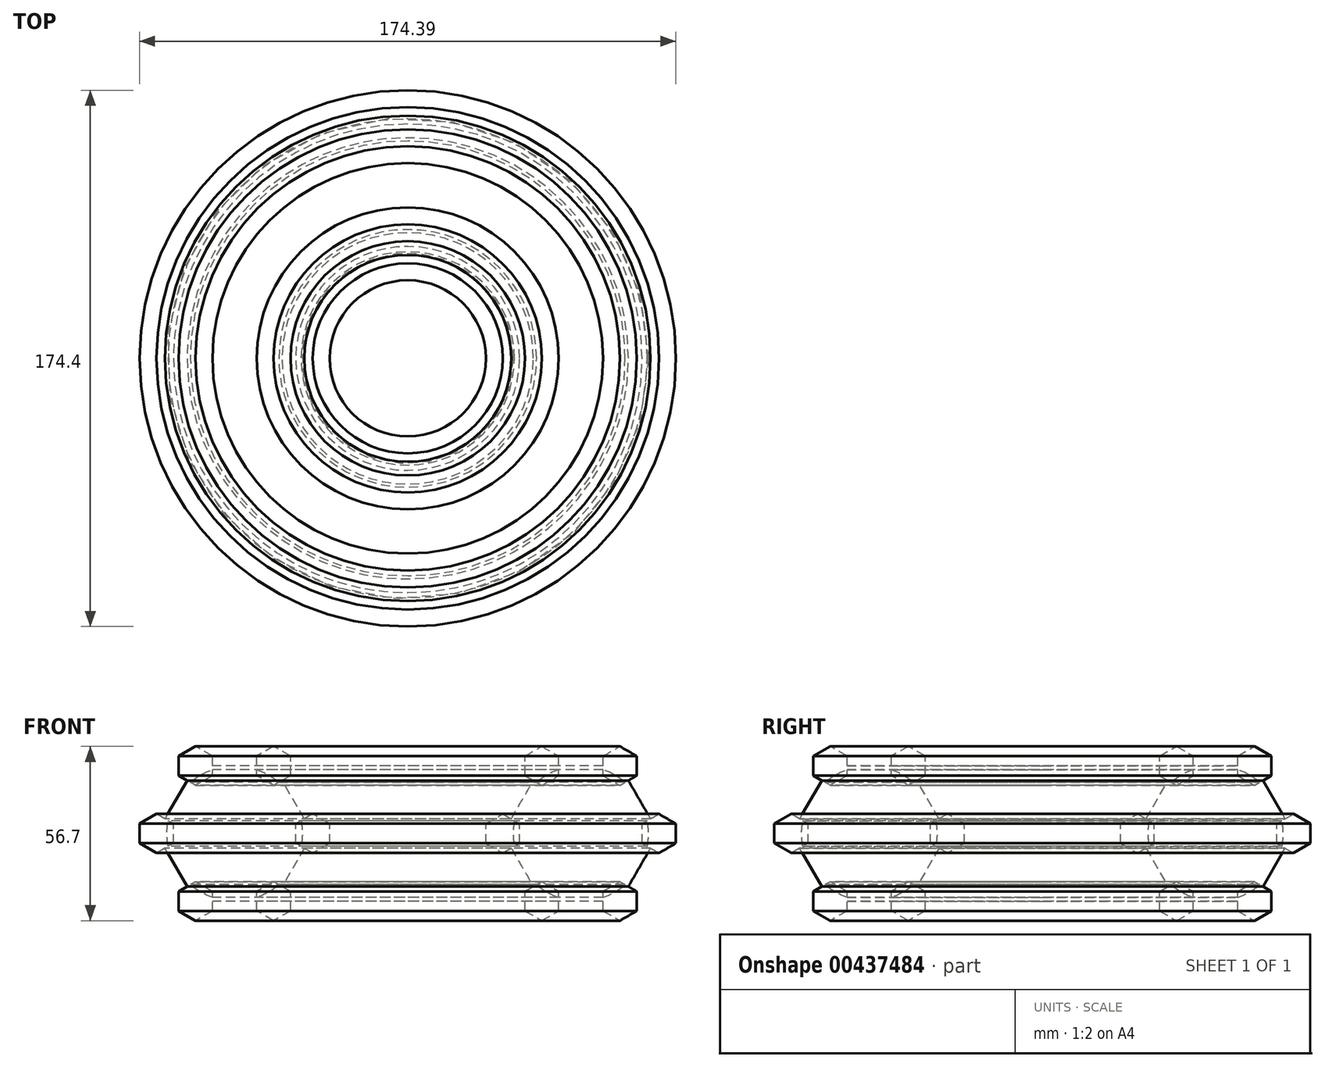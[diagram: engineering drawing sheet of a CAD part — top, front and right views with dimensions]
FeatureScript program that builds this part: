
annotation { "Feature Type Name" : "Feature", "Feature Type Description" : "" }
export const myFeature = defineFeature(function(context is Context, id is Id, definition is map)
    precondition{}
    {
        {
            var Q0;
            Q0=qCreatedBy(makeId("Front.planeOp"),FACE);
            var sketch = newSketch(context, id + "F0", { "sketchPlane" : qUnion([Q0])});
            skCircle(sketch, "E0.cCircle", {"center": v(-30.78, 15.87) * mm, "radius": 22 * mm});
            skLineSegment(sketch, "E0.0", {"start": v(-43.48, 37.87) * mm, "end": v(-18.08, 37.87) * mm});
            skLineSegment(sketch, "E0.1", {"start": v(-18.08, 37.87) * mm, "end": v(-5.38, 15.87) * mm});
            skLineSegment(sketch, "E0.2", {"start": v(-5.38, 15.87) * mm, "end": v(-18.08, -6.13) * mm});
            skLineSegment(sketch, "E0.3", {"start": v(-18.08, -6.13) * mm, "end": v(-43.48, -6.13) * mm});
            skLineSegment(sketch, "E0.4", {"start": v(-43.48, -6.13) * mm, "end": v(-56.18, 15.87) * mm});
            skLineSegment(sketch, "E0.5", {"start": v(-56.18, 15.87) * mm, "end": v(-43.48, 37.87) * mm});
            skPoint(sketch, "E0.0.midPoint", {"position": v(-30.78, 37.87) * mm});
            skCircle(sketch, "E1.cCircle", {"center": v(-43.48, 37.87) * mm, "radius": 5.5 * mm, "construction": true});
            skLineSegment(sketch, "E1.0", {"start": v(-48.98, 41.04) * mm, "end": v(-43.48, 44.22) * mm});
            skLineSegment(sketch, "E1.1", {"start": v(-43.48, 44.22) * mm, "end": v(-37.99, 41.04) * mm});
            skLineSegment(sketch, "E1.2", {"start": v(-37.99, 41.04) * mm, "end": v(-37.99, 34.7) * mm});
            skLineSegment(sketch, "E1.3", {"start": v(-37.99, 34.7) * mm, "end": v(-43.48, 31.52) * mm});
            skLineSegment(sketch, "E1.4", {"start": v(-43.48, 31.52) * mm, "end": v(-48.98, 34.7) * mm});
            skLineSegment(sketch, "E1.5", {"start": v(-48.98, 34.7) * mm, "end": v(-48.98, 41.04) * mm});
            skPoint(sketch, "E1.0.midPoint", {"position": v(-46.23, 42.63) * mm});
            skLineSegment(sketch, "E2", {"start": v(-46.23, 42.63) * mm, "end": v(-43.48, 37.87) * mm, "construction": true});
            skLineSegment(sketch, "E3.1.0", {"start": v(-61.68, 19.04) * mm, "end": v(-56.18, 22.22) * mm});
            skLineSegment(sketch, "E3.1.1", {"start": v(-56.18, 22.22) * mm, "end": v(-50.69, 19.04) * mm});
            skLineSegment(sketch, "E3.1.2", {"start": v(-50.69, 19.04) * mm, "end": v(-50.69, 12.7) * mm});
            skLineSegment(sketch, "E3.1.3", {"start": v(-50.69, 12.7) * mm, "end": v(-56.18, 9.52) * mm});
            skLineSegment(sketch, "E3.1.4", {"start": v(-56.18, 9.52) * mm, "end": v(-61.68, 12.7) * mm});
            skLineSegment(sketch, "E3.1.5", {"start": v(-61.68, 12.7) * mm, "end": v(-61.68, 19.04) * mm});
            skLineSegment(sketch, "E3.2.0", {"start": v(-48.98, -9.3) * mm, "end": v(-48.98, -2.95) * mm});
            skLineSegment(sketch, "E3.2.1", {"start": v(-48.98, -2.95) * mm, "end": v(-43.48, 0.22) * mm});
            skLineSegment(sketch, "E3.2.2", {"start": v(-43.48, 0.22) * mm, "end": v(-37.99, -2.95) * mm});
            skLineSegment(sketch, "E3.2.3", {"start": v(-37.99, -2.95) * mm, "end": v(-37.99, -9.3) * mm});
            skLineSegment(sketch, "E3.2.4", {"start": v(-37.99, -9.3) * mm, "end": v(-43.48, -12.48) * mm});
            skLineSegment(sketch, "E3.2.5", {"start": v(-43.48, -12.48) * mm, "end": v(-48.98, -9.3) * mm});
            skLineSegment(sketch, "E3.3.0", {"start": v(-18.08, -12.48) * mm, "end": v(-23.58, -9.3) * mm});
            skLineSegment(sketch, "E3.3.1", {"start": v(-23.58, -9.3) * mm, "end": v(-23.58, -2.95) * mm});
            skLineSegment(sketch, "E3.3.2", {"start": v(-23.58, -2.95) * mm, "end": v(-18.08, 0.22) * mm});
            skLineSegment(sketch, "E3.3.3", {"start": v(-18.08, 0.22) * mm, "end": v(-12.59, -2.95) * mm});
            skLineSegment(sketch, "E3.3.4", {"start": v(-12.59, -2.95) * mm, "end": v(-12.59, -9.3) * mm});
            skLineSegment(sketch, "E3.3.5", {"start": v(-12.59, -9.3) * mm, "end": v(-18.08, -12.48) * mm});
            skLineSegment(sketch, "E3.4.0", {"start": v(0.11, 12.7) * mm, "end": v(-5.38, 9.52) * mm});
            skLineSegment(sketch, "E3.4.1", {"start": v(-5.38, 9.52) * mm, "end": v(-10.88, 12.7) * mm});
            skLineSegment(sketch, "E3.4.2", {"start": v(-10.88, 12.7) * mm, "end": v(-10.88, 19.04) * mm});
            skLineSegment(sketch, "E3.4.3", {"start": v(-10.88, 19.04) * mm, "end": v(-5.38, 22.22) * mm});
            skLineSegment(sketch, "E3.4.4", {"start": v(-5.38, 22.22) * mm, "end": v(0.11, 19.04) * mm});
            skLineSegment(sketch, "E3.4.5", {"start": v(0.11, 19.04) * mm, "end": v(0.11, 12.7) * mm});
            skLineSegment(sketch, "E3.5.0", {"start": v(-12.59, 41.04) * mm, "end": v(-12.59, 34.7) * mm});
            skLineSegment(sketch, "E3.5.1", {"start": v(-12.59, 34.7) * mm, "end": v(-18.08, 31.52) * mm});
            skLineSegment(sketch, "E3.5.2", {"start": v(-18.08, 31.52) * mm, "end": v(-23.58, 34.7) * mm});
            skLineSegment(sketch, "E3.5.3", {"start": v(-23.58, 34.7) * mm, "end": v(-23.58, 41.04) * mm});
            skLineSegment(sketch, "E3.5.4", {"start": v(-23.58, 41.04) * mm, "end": v(-18.08, 44.22) * mm});
            skLineSegment(sketch, "E3.5.5", {"start": v(-18.08, 44.22) * mm, "end": v(-12.59, 41.04) * mm});
            skLineSegment(sketch, "E4", {"start": v(25.51, 64.86) * mm, "end": v(25.51, -30.56) * mm, "construction": true});
            skLineSegment(sketch, "E5", {"start": v(0.11, 12.7) * mm, "end": v(25.51, 12.7) * mm, "construction": true});
            skSolve(sketch);
        }
        {
            var Q0;
            Q0 = qSketchRegion(id + "F0", true);
            var Q1;
            Q1=sQuery(id+"F0.wireOp",EDGE,"E4");
            revolve(context, id + "F1", {"entities" : qUnion([Q0]), "axis" : qUnion([Q1]), "revolveType" : RevolveType.FULL});
        }
    });
